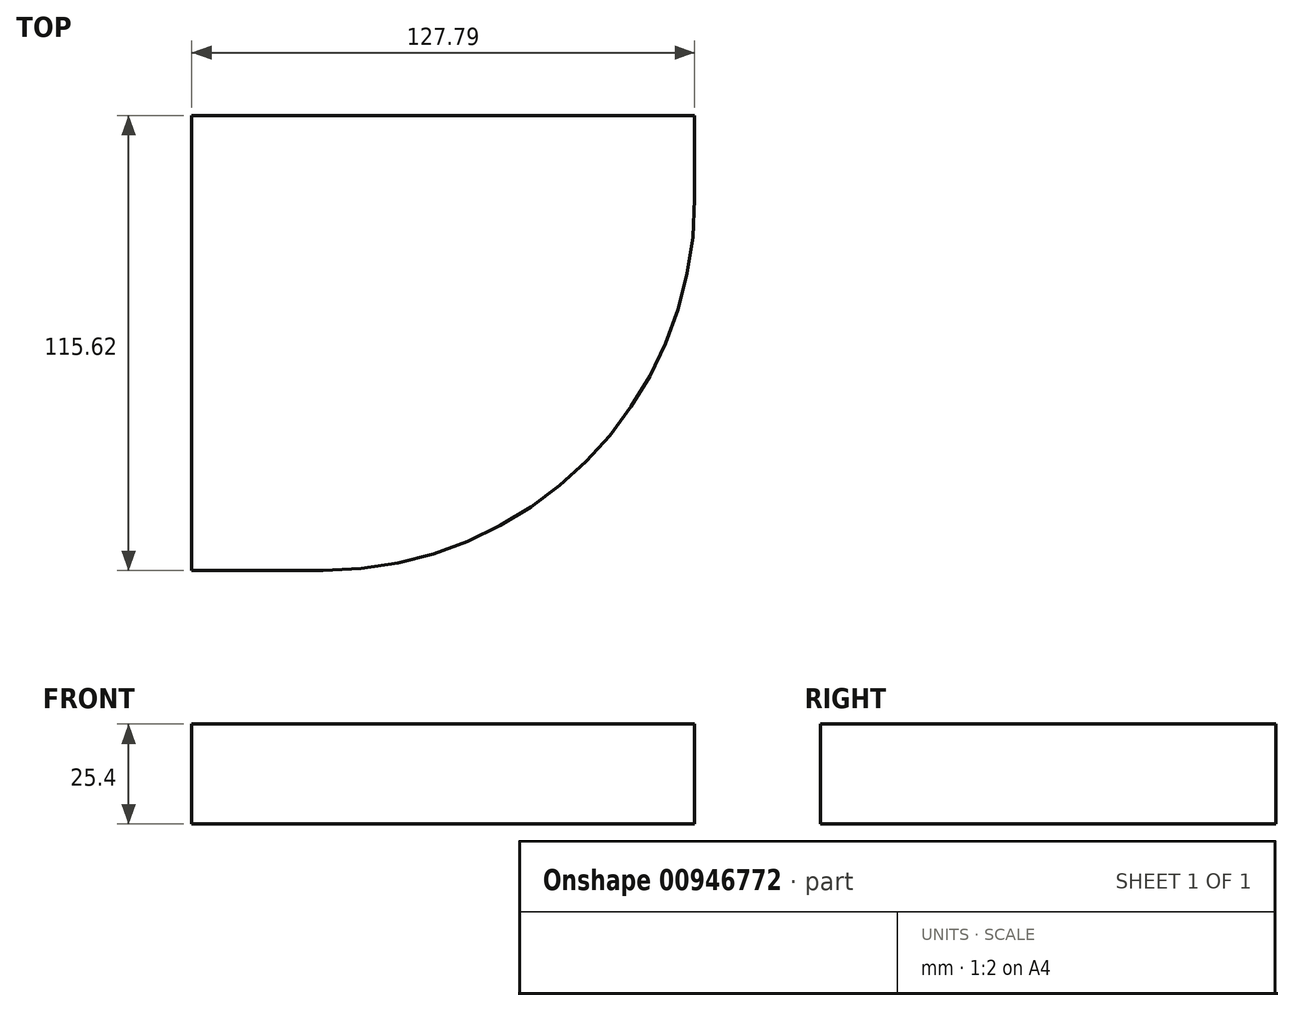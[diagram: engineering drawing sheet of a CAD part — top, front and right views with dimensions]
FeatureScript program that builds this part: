
annotation { "Feature Type Name" : "Feature", "Feature Type Description" : "" }
export const myFeature = defineFeature(function(context is Context, id is Id, definition is map)
    precondition{}
    {
        {
            var Q0;
            Q0=qCreatedBy(makeId("Top.planeOp"),FACE);
            var sketch = newSketch(context, id + "F0", { "sketchPlane" : qUnion([Q0])});
            skLineSegment(sketch, "E0.bottom", {"start": v(-66.47, 52.28) * mm, "end": v(61.32, 52.28) * mm});
            skLineSegment(sketch, "E0.top", {"start": v(-66.47, -63.34) * mm, "end": v(61.32, -63.34) * mm});
            skLineSegment(sketch, "E0.left", {"start": v(-66.47, 52.28) * mm, "end": v(-66.47, -63.34) * mm});
            skLineSegment(sketch, "E0.right", {"start": v(61.32, 52.28) * mm, "end": v(61.32, -63.34) * mm});
            skSolve(sketch);
        }
        {
            var Q0;
            Q0=makeQuery(id+"F0.imprint","IMPRINT",FACE,{"disambiguationData":[TD([[makeQuery(id+"F0.imprint","IMPRINT",EDGE,{"derivedFrom":sQuery(id+"F0.wireOp",EDGE,"E0.bottom")}),-1.0]])]});
            extrude(context, id + "F1", {"entities" : qUnion([Q0]), "depth" : 25.4 * mm, "offsetDistance" : 25.4 * mm});
        }
        {
            var Q0;
            Q0=makeQuery(id+"F1.opExtrude","SWEPT_EDGE",EDGE,{"disambiguationData":[OSD([sQuery(id+"F0.wireOp",EDGE,"E0.top"),sQuery(id+"F0.wireOp",EDGE,"E0.right")])]});
            fillet(context, id + "F2", {"entities" : qUnion([Q0]), "radius" : 94.43 * mm, "tangentPropagation" : true, "allowEdgeOverflow" : false});
        }
    });
